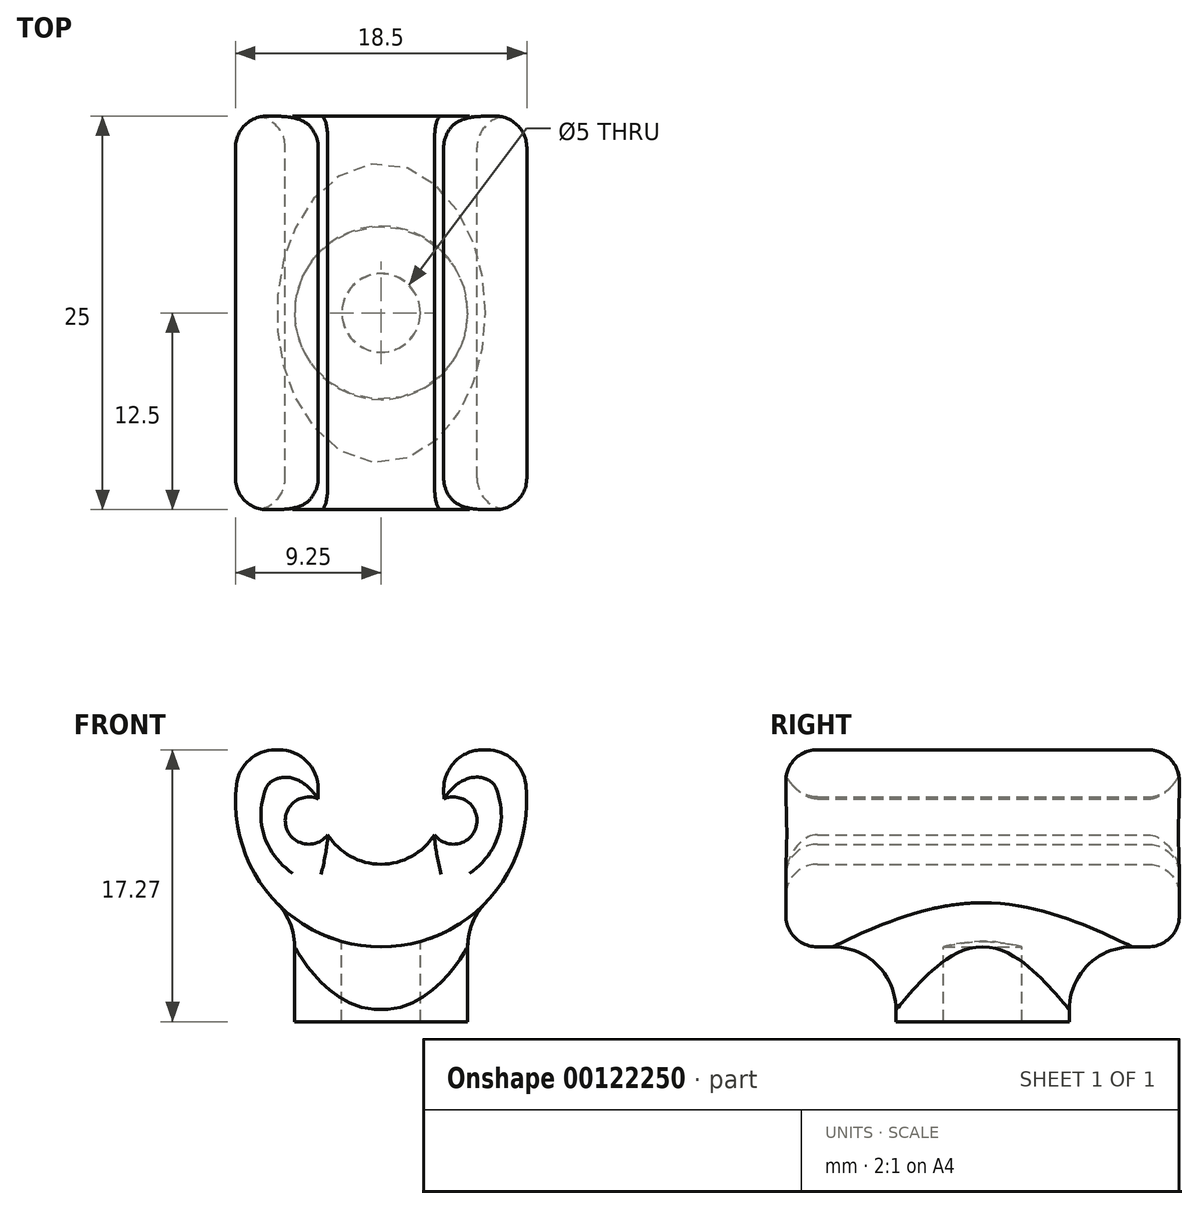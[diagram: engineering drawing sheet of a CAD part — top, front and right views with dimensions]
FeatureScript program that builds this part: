
annotation { "Feature Type Name" : "Feature", "Feature Type Description" : "" }
export const myFeature = defineFeature(function(context is Context, id is Id, definition is map)
    precondition{}
    {
        {
            var Q0;
            Q0=qCreatedBy(makeId("Front.planeOp"),FACE);
            var sketch = newSketch(context, id + "F0", { "sketchPlane" : qUnion([Q0])});
            skCircle(sketch, "E0", {"center": v(0, 0) * mm, "radius": 3.25 * mm, "construction": true});
            skCircle(sketch, "E1.0", {"center": v(0, 0) * mm, "radius": 4.75 * mm, "construction": true});
            skLineSegment(sketch, "E2", {"start": v(0, 0) * mm, "end": v(-11.05, -2.96) * mm, "construction": true});
            skCircle(sketch, "E3", {"center": v(-4.59, -1.23) * mm, "radius": 1.5 * mm, "construction": true});
            skCircle(sketch, "E4.0", {"center": v(0, 0) * mm, "radius": 9.25 * mm, "construction": true});
            skLineSegment(sketch, "E5", {"start": v(0, 9.25) * mm, "end": v(0, -17.08) * mm, "construction": true});
            skCircle(sketch, "E6.MirrorC", {"center": v(4.59, -1.23) * mm, "radius": 1.5 * mm, "construction": true});
            skCircle(sketch, "E7.0", {"center": v(0, 0) * mm, "radius": 4 * mm, "construction": true});
            skLineSegment(sketch, "E8", {"start": v(-4.6, 0.27) * mm, "end": v(4.59, 0.27) * mm, "construction": true});
            skLineSegment(sketch, "E9.0", {"start": v(-8.65, 3.27) * mm, "end": v(8.65, 3.27) * mm, "construction": true});
            skSolve(sketch);
        }
        {
            var Q0;
            Q0=qCreatedBy(makeId("Front.planeOp"),FACE);
            var sketch = newSketch(context, id + "F1", { "sketchPlane" : qUnion([Q0])});
            skArc(sketch, "E10.0", {"start": v(-9.19, 1.06) * mm, "mid": v(0, -9.25) * mm, "end": v(9.19, 1.06) * mm});
            skLineSegment(sketch, "E11.0", {"start": v(-6.7, 3.27) * mm, "end": v(-6.5, 3.27) * mm});
            skArc(sketch, "E12.0", {"start": v(-4, 0.15) * mm, "mid": v(-6.04, -1.62) * mm, "end": v(-3.39, -2.13) * mm});
            skArc(sketch, "E13.0", {"start": v(4, 0.15) * mm, "mid": v(6.04, -1.62) * mm, "end": v(3.39, -2.13) * mm});
            skPoint(sketch, "E14.orphan", {"position": v(0, 9.25) * mm});
            skLineSegment(sketch, "E15.trimOffspring", {"start": v(6.48, 3.27) * mm, "end": v(6.7, 3.27) * mm});
            skArc(sketch, "E16.trimOffspring", {"start": v(-3.39, -2.13) * mm, "mid": v(0, -4) * mm, "end": v(3.39, -2.13) * mm});
            skLineSegment(sketch, "E17", {"start": v(-4, 0.15) * mm, "end": v(-4, 0.77) * mm});
            skLineSegment(sketch, "E18", {"start": v(4, 0.15) * mm, "end": v(3.98, 0.68) * mm});
            skPoint(sketch, "E19.visualSharp", {"position": v(-4, 3.27) * mm});
            skArc(sketch, "E19.filletArc", {"start": v(-4, 0.77) * mm, "mid": v(-4.73, 2.54) * mm, "end": v(-6.5, 3.27) * mm});
            skPoint(sketch, "E20.visualSharp", {"position": v(-8.65, 3.27) * mm});
            skArc(sketch, "E20.filletArc", {"start": v(-6.7, 3.27) * mm, "mid": v(-8.37, 2.64) * mm, "end": v(-9.19, 1.06) * mm});
            skPoint(sketch, "E21.visualSharp", {"position": v(3.88, 3.27) * mm});
            skArc(sketch, "E21.filletArc", {"start": v(6.48, 3.27) * mm, "mid": v(4.68, 2.5) * mm, "end": v(3.98, 0.68) * mm});
            skPoint(sketch, "E22.visualSharp", {"position": v(8.65, 3.27) * mm});
            skArc(sketch, "E22.filletArc", {"start": v(9.19, 1.06) * mm, "mid": v(8.37, 2.64) * mm, "end": v(6.7, 3.27) * mm});
            skSolve(sketch);
        }
        {
            var Q0;
            Q0=makeQuery(id+"F1.imprint","IMPRINT",FACE,{"disambiguationData":[TD([[makeQuery(id+"F1.imprint","IMPRINT",EDGE,{"derivedFrom":sQuery(id+"F1.wireOp",EDGE,"E10.0")}),1.0]])]});
            extrude(context, id + "F2", {"entities" : qUnion([Q0]), "endBound" : BoundingType.SYMMETRIC, "depth" : 25 * mm});
        }
        {
            var Q0;
            Q0=qCreatedBy(makeId("Top.planeOp"),FACE);
            cPlane(context, id + "F3", {"entities" : qUnion([Q0]), "cplaneType" : CPlaneType.OFFSET, "offset" : 7 * mm, "oppositeDirection" : true, "width" : 150 * mm, "height" : 150 * mm});
        }
        {
            var Q0;
            Q0=qCreatedBy(id+"F3.planeOp",FACE);
            var sketch = newSketch(context, id + "F4", { "sketchPlane" : qUnion([Q0])});
            skCircle(sketch, "E23", {"center": v(0, 0) * mm, "radius": 2.5 * mm});
            skCircle(sketch, "E24.0", {"center": v(0, 0) * mm, "radius": 5.5 * mm});
            skSolve(sketch);
        }
        {
            var Q0;
            Q0=makeQuery(id+"F4.imprint","IMPRINT",FACE,{"disambiguationData":[TD([[makeQuery(id+"F4.imprint","IMPRINT",EDGE,{"derivedFrom":sQuery(id+"F4.wireOp",EDGE,"E23")}),-1.0]])]});
            var Q1;
            Q1=sQuery(id+"F4.wireOp",EDGE,"E24.0");
            var Q2;
            Q2=sQuery(id+"F4.wireOp",EDGE,"E23");
            extrude(context, id + "F5", {"entities" : qUnion([Q0]), "surfaceEntities" : qUnion([Q1, Q2]), "oppositeDirection" : true, "depth" : 7 * mm});
        }
        {
            var Q0;
            Q0=makeQuery(id+"F2.opExtrude","SWEPT_BODY",BODY,{"disambiguationData":[OSD([sQuery(id+"F1.wireOp",EDGE,"E10.0"),sQuery(id+"F1.wireOp",EDGE,"E11.0"),sQuery(id+"F1.wireOp",EDGE,"E12.0"),sQuery(id+"F1.wireOp",EDGE,"E13.0"),sQuery(id+"F1.wireOp",EDGE,"E15.trimOffspring"),sQuery(id+"F1.wireOp",EDGE,"E16.trimOffspring"),sQuery(id+"F1.wireOp",EDGE,"E17"),sQuery(id+"F1.wireOp",EDGE,"E18"),sQuery(id+"F1.wireOp",EDGE,"E19.filletArc"),sQuery(id+"F1.wireOp",EDGE,"E20.filletArc"),sQuery(id+"F1.wireOp",EDGE,"E21.filletArc"),sQuery(id+"F1.wireOp",EDGE,"E22.filletArc")])]});
            var Q1;
            Q1=makeQuery(id+"F5.opExtrude","SWEPT_BODY",BODY,{"disambiguationData":[OSD([sQuery(id+"F4.wireOp",EDGE,"E23"),sQuery(id+"F4.wireOp",EDGE,"E24.0")])]});
            booleanBodies(context, id + "F6", {"operationType" : BooleanOperationType.UNION, "tools" : qUnion([Q0, Q1])});
        }
        {
            var Q0;
            Q0=makeQuery(id+"F6.opBoolean","INTERSECT",EDGE,{"derivedFrom":[makeQuery(id+"F2.opExtrude","SWEPT_FACE",FACE,{"disambiguationData":[OSD([sQuery(id+"F1.wireOp",EDGE,"E10.0")])]}),makeQuery(id+"F5.opExtrude","SWEPT_FACE",FACE,{"disambiguationData":[OSD([sQuery(id+"F4.wireOp",EDGE,"E24.0")])]})]});
            fillet(context, id + "F7", {"entities" : qUnion([Q0]), "radius" : 4 * mm, "tangentPropagation" : true, "allowEdgeOverflow" : false});
        }
        {
            var Q0;
            Q0=makeQuery(id+"F2.opExtrude","CAP_FACE",FACE,{"disambiguationData":[OSD([sQuery(id+"F1.wireOp",EDGE,"E10.0"),sQuery(id+"F1.wireOp",EDGE,"E11.0"),sQuery(id+"F1.wireOp",EDGE,"E12.0"),sQuery(id+"F1.wireOp",EDGE,"E13.0"),sQuery(id+"F1.wireOp",EDGE,"E15.trimOffspring"),sQuery(id+"F1.wireOp",EDGE,"E16.trimOffspring"),sQuery(id+"F1.wireOp",EDGE,"E17"),sQuery(id+"F1.wireOp",EDGE,"E18"),sQuery(id+"F1.wireOp",EDGE,"E19.filletArc"),sQuery(id+"F1.wireOp",EDGE,"E20.filletArc"),sQuery(id+"F1.wireOp",EDGE,"E21.filletArc"),sQuery(id+"F1.wireOp",EDGE,"E22.filletArc")])],"isStart":true});
            var Q1;
            Q1=makeQuery(id+"F2.opExtrude","CAP_FACE",FACE,{"disambiguationData":[OSD([sQuery(id+"F1.wireOp",EDGE,"E10.0"),sQuery(id+"F1.wireOp",EDGE,"E11.0"),sQuery(id+"F1.wireOp",EDGE,"E12.0"),sQuery(id+"F1.wireOp",EDGE,"E13.0"),sQuery(id+"F1.wireOp",EDGE,"E15.trimOffspring"),sQuery(id+"F1.wireOp",EDGE,"E16.trimOffspring"),sQuery(id+"F1.wireOp",EDGE,"E17"),sQuery(id+"F1.wireOp",EDGE,"E18"),sQuery(id+"F1.wireOp",EDGE,"E19.filletArc"),sQuery(id+"F1.wireOp",EDGE,"E20.filletArc"),sQuery(id+"F1.wireOp",EDGE,"E21.filletArc"),sQuery(id+"F1.wireOp",EDGE,"E22.filletArc")])],"isStart":false});
            fillet(context, id + "F8", {"entities" : qUnion([Q0, Q1]), "radius" : 2 * mm, "tangentPropagation" : true, "allowEdgeOverflow" : false});
        }
    });
